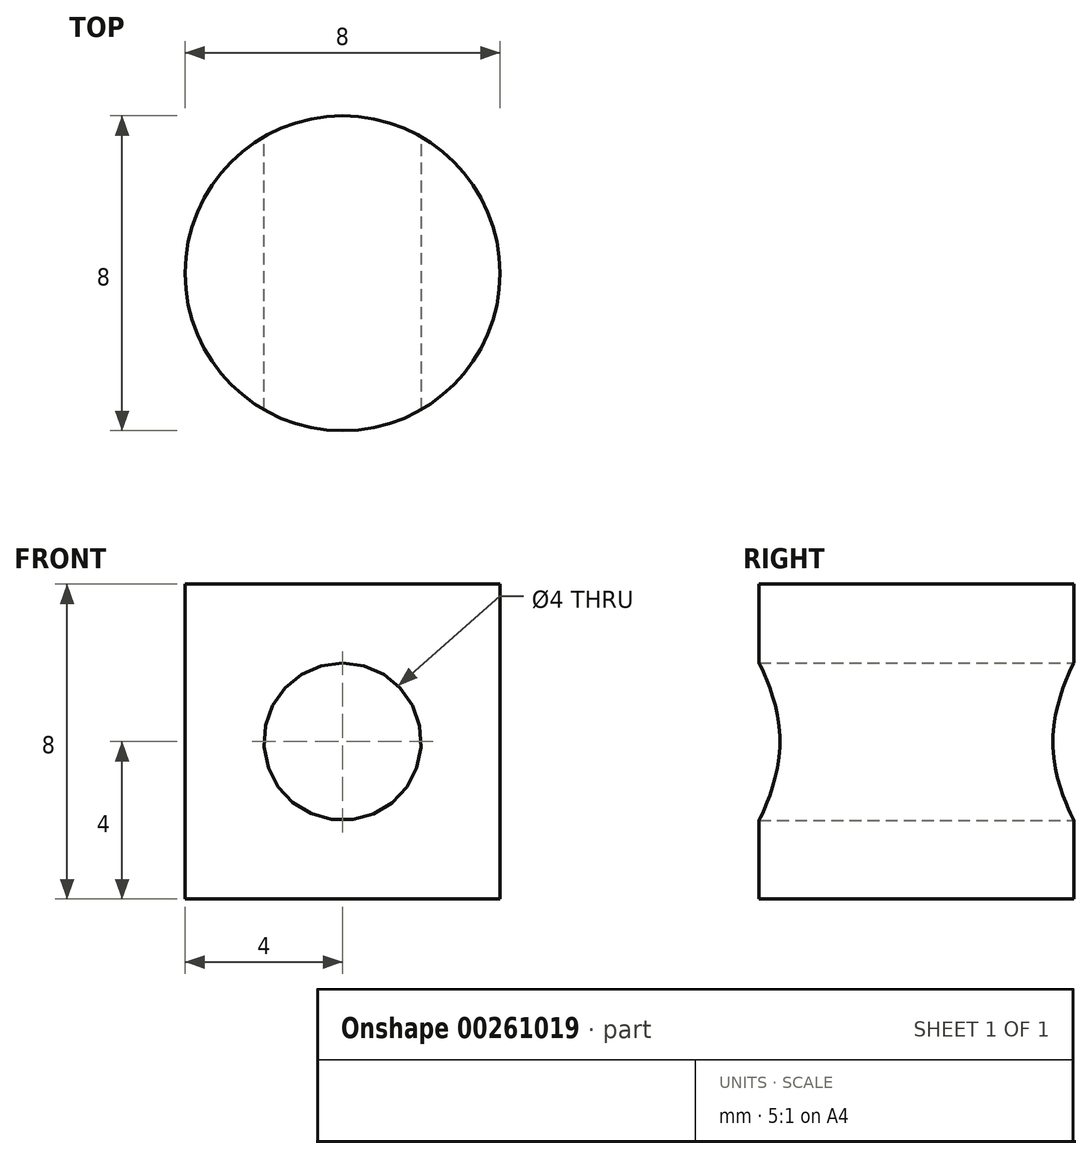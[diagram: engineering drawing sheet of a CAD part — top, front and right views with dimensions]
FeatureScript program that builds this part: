
annotation { "Feature Type Name" : "Feature", "Feature Type Description" : "" }
export const myFeature = defineFeature(function(context is Context, id is Id, definition is map)
    precondition{}
    {
        {
            var Q0;
            Q0=qCreatedBy(makeId("Top.planeOp"),FACE);
            var sketch = newSketch(context, id + "F0", { "sketchPlane" : qUnion([Q0])});
            skCircle(sketch, "E0", {"center": v(0, 0) * mm, "radius": 4 * mm});
            skSolve(sketch);
        }
        {
            var Q0;
            Q0 = qSketchRegion(id + "F0", true);
            extrude(context, id + "F1", {"entities" : qUnion([Q0]), "endBound" : BoundingType.SYMMETRIC, "depth" : 8 * mm});
        }
        {
            var Q0;
            Q0=qCreatedBy(makeId("Front.planeOp"),FACE);
            var sketch = newSketch(context, id + "F2", { "sketchPlane" : qUnion([Q0])});
            skCircle(sketch, "E1", {"center": v(0, 0) * mm, "radius": 2 * mm});
            skSolve(sketch);
        }
        {
            var Q0;
            Q0 = qSketchRegion(id + "F2", true);
            extrude(context, id + "F3", {"entities" : qUnion([Q0]), "operationType" : NewBodyOperationType.REMOVE, "endBound" : BoundingType.SYMMETRIC, "depth" : 8 * mm});
        }
    });
